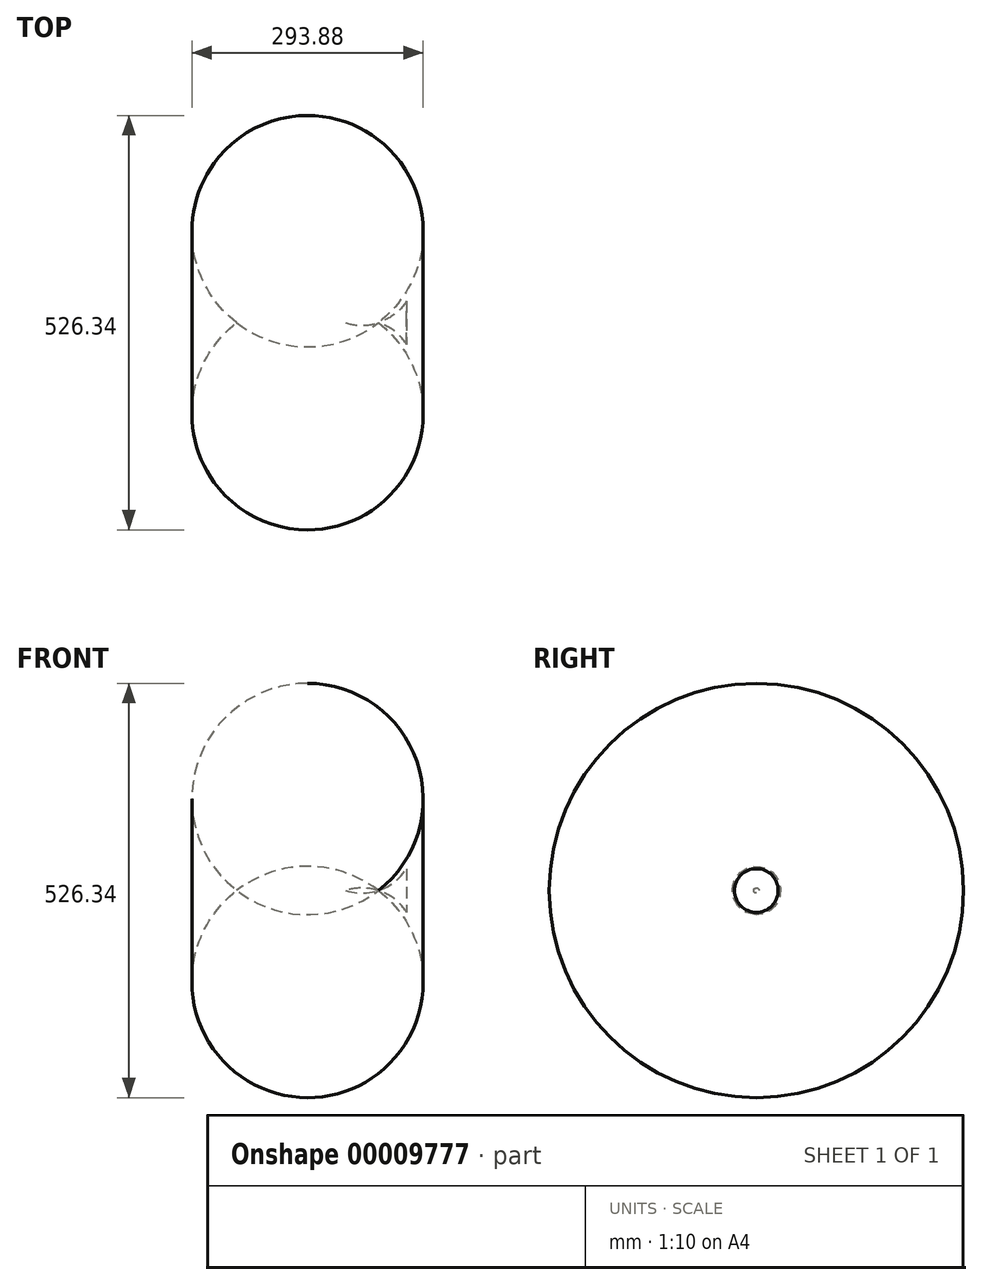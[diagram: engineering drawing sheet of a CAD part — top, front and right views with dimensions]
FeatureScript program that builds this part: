
annotation { "Feature Type Name" : "Feature", "Feature Type Description" : "" }
export const myFeature = defineFeature(function(context is Context, id is Id, definition is map)
    precondition{}
    {
        {
            var Q0;
            Q0=qCreatedBy(makeId("Top.planeOp"),FACE);
            var sketch = newSketch(context, id + "F0", { "sketchPlane" : qUnion([Q0])});
            skLineSegment(sketch, "E0", {"start": v(-85.96, 0) * mm, "end": v(93.85, 0) * mm});
            skArc(sketch, "E1", {"start": v(93.85, 0) * mm, "mid": v(3.95, 30.71) * mm, "end": v(-85.96, 0) * mm});
            skLineSegment(sketch, "E2", {"start": v(93.85, 0) * mm, "end": v(129.93, 27.7) * mm, "construction": true});
            skLineSegment(sketch, "E3", {"start": v(93.85, 0) * mm, "end": v(129.93, 0) * mm});
            skArc(sketch, "E4", {"start": v(93.85, 0) * mm, "mid": v(114.3, 10.72) * mm, "end": v(129.93, 27.7) * mm});
            skLineSegment(sketch, "E5", {"start": v(129.93, 27.7) * mm, "end": v(129.93, 0) * mm});
            skArc(sketch, "E6.0.MirrorCS", {"start": v(93.85, 0) * mm, "mid": v(114.3, -10.72) * mm, "end": v(129.93, -27.7) * mm});
            skLineSegment(sketch, "E7.0.MirrorCS", {"start": v(129.93, -27.7) * mm, "end": v(129.93, 0) * mm});
            skArc(sketch, "E8.0.MirrorCS", {"start": v(93.85, 0) * mm, "mid": v(3.95, -30.71) * mm, "end": v(-85.96, 0) * mm});
            skSolve(sketch);
        }
        {
            var Q0;
            Q0=makeQuery(id+"F0.imprint","IMPRINT",FACE,{"disambiguationData":[TD([[makeQuery(id+"F0.imprint","IMPRINT",EDGE,{"derivedFrom":sQuery(id+"F0.wireOp",EDGE,"E0")}),1.0]])]});
            var Q1;
            Q1=makeQuery(id+"F0.imprint","IMPRINT",FACE,{"disambiguationData":[TD([[makeQuery(id+"F0.imprint","IMPRINT",EDGE,{"derivedFrom":sQuery(id+"F0.wireOp",EDGE,"E3")}),1.0]])]});
            var Q2;
            Q2=sQuery(id+"F0.wireOp",EDGE,"E0");
            revolve(context, id + "F1", {"entities" : qUnion([Q0, Q1]), "axis" : qUnion([Q2]), "revolveType" : RevolveType.FULL});
        }
    });
